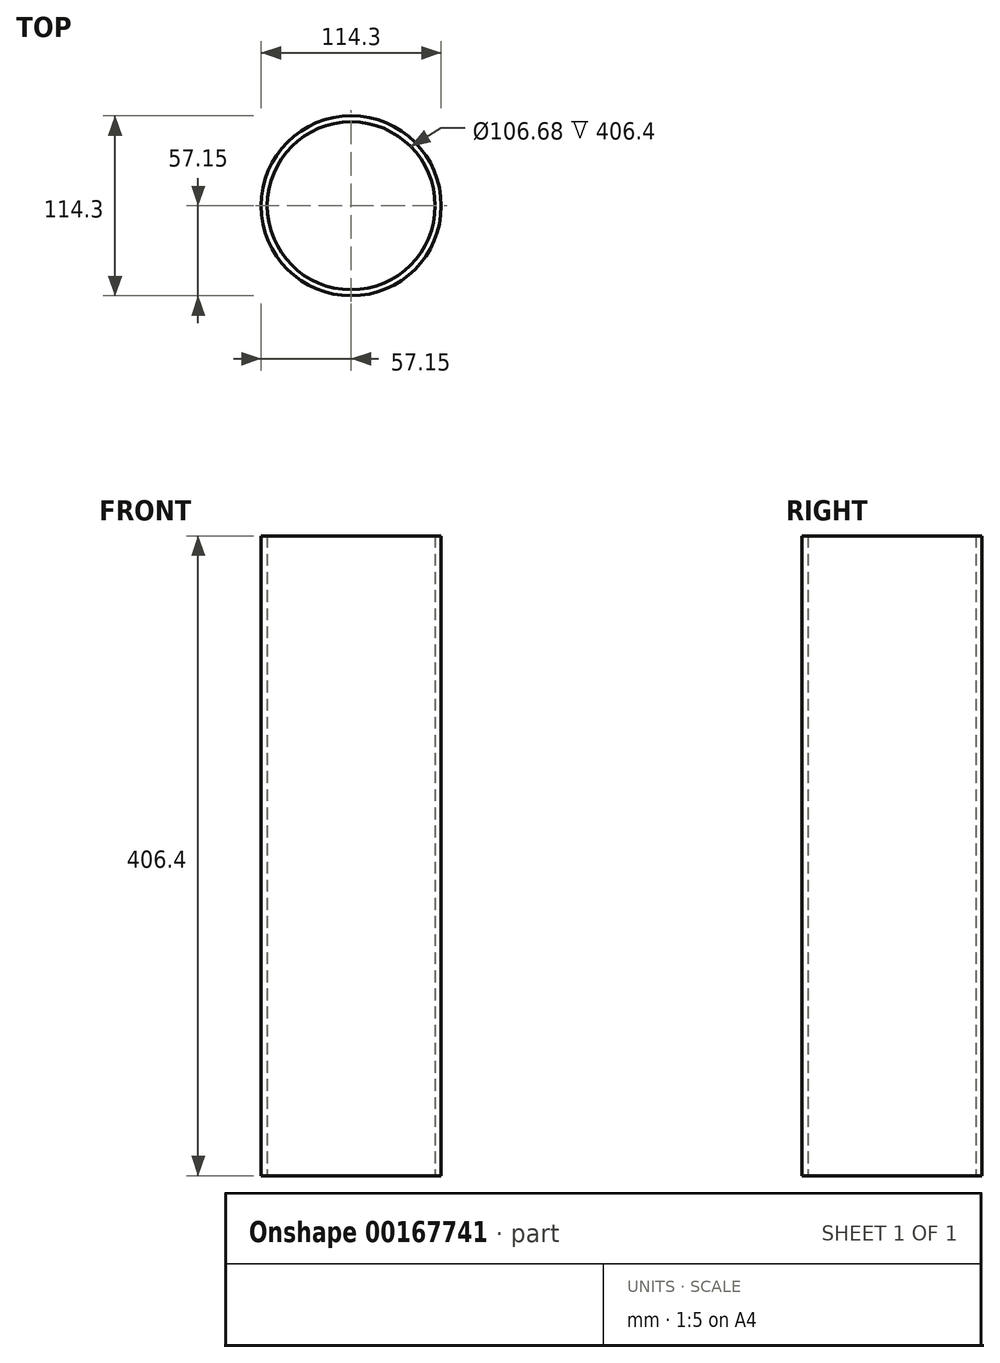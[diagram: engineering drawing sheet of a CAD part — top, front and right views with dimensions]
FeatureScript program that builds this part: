
annotation { "Feature Type Name" : "Feature", "Feature Type Description" : "" }
export const myFeature = defineFeature(function(context is Context, id is Id, definition is map)
    precondition{}
    {
        {
            var Q0;
            Q0=qCreatedBy(makeId("Top.planeOp"),FACE);
            var sketch = newSketch(context, id + "F0", { "sketchPlane" : qUnion([Q0])});
            skCircle(sketch, "E0", {"center": v(0, 0) * mm, "radius": 57.15 * mm});
            skCircle(sketch, "E1", {"center": v(0, 0) * mm, "radius": 53.34 * mm});
            skSolve(sketch);
        }
        {
            var Q0;
            Q0=makeQuery(id+"F0.imprint","IMPRINT",FACE,{"disambiguationData":[TD([[makeQuery(id+"F0.imprint","IMPRINT",EDGE,{"derivedFrom":sQuery(id+"F0.wireOp",EDGE,"E0")}),1.0]])]});
            extrude(context, id + "F1", {"entities" : qUnion([Q0]), "depth" : 406.4 * mm});
        }
    });
